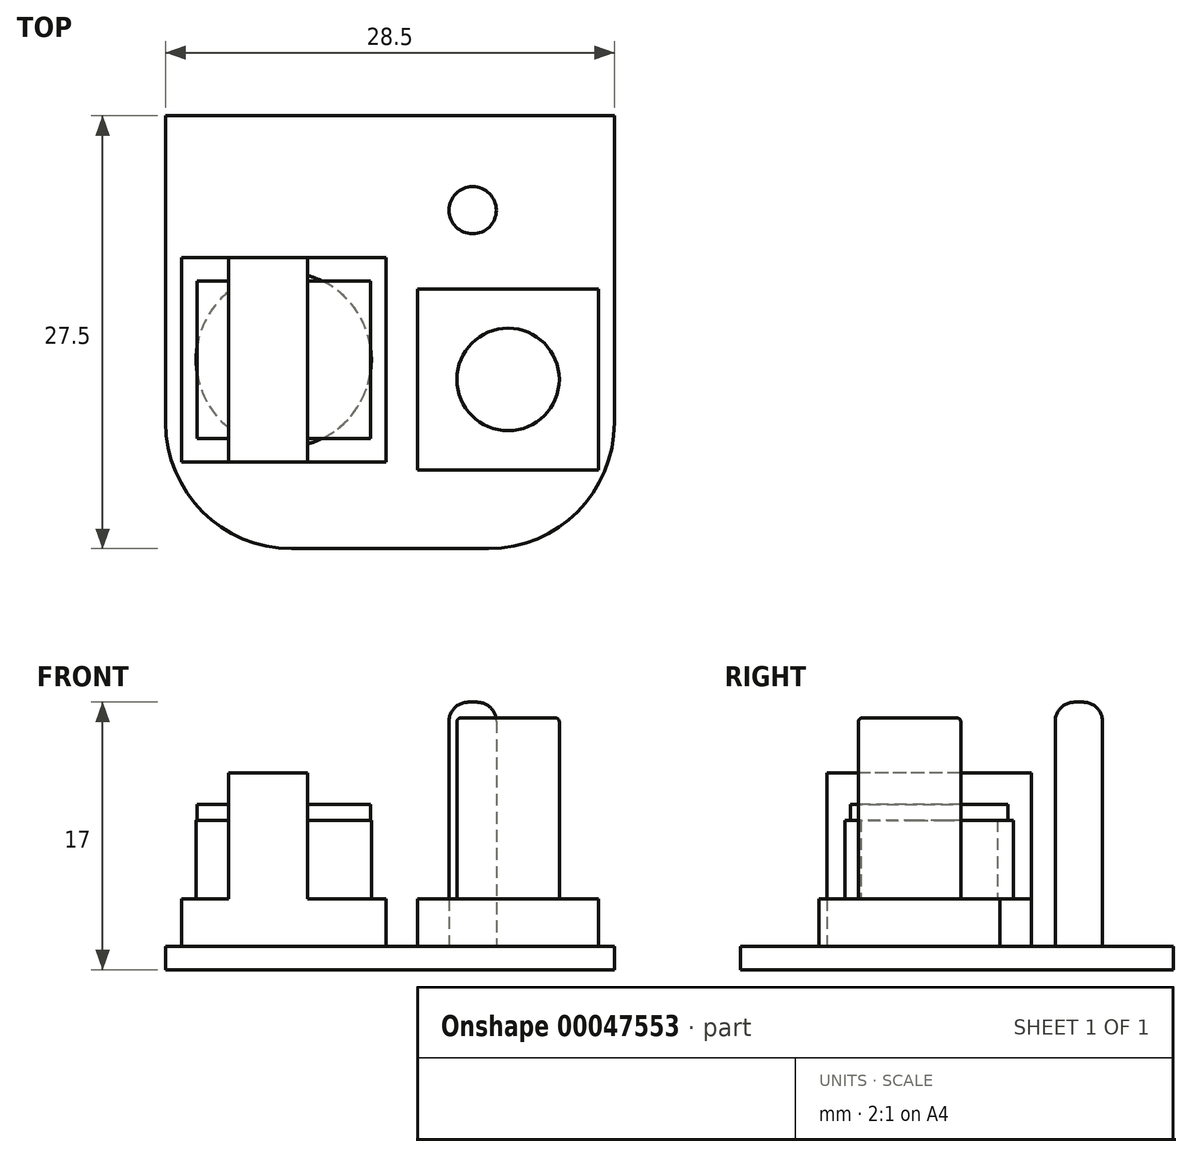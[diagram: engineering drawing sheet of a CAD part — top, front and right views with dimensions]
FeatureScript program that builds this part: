
annotation { "Feature Type Name" : "Feature", "Feature Type Description" : "" }
export const myFeature = defineFeature(function(context is Context, id is Id, definition is map)
    precondition{}
    {
        {
            var Q0;
            Q0=qCreatedBy(makeId("Top.planeOp"),FACE);
            var sketch = newSketch(context, id + "F0", { "sketchPlane" : qUnion([Q0])});
            skLineSegment(sketch, "E0.bottom", {"start": v(-14.25, 13.75) * mm, "end": v(14.25, 13.75) * mm});
            skLineSegment(sketch, "E0.top", {"start": v(-14.25, -13.75) * mm, "end": v(14.25, -13.75) * mm});
            skLineSegment(sketch, "E0.left", {"start": v(-14.25, 13.75) * mm, "end": v(-14.25, -13.75) * mm});
            skLineSegment(sketch, "E0.right", {"start": v(14.25, 13.75) * mm, "end": v(14.25, -13.75) * mm});
            skSolve(sketch);
        }
        {
            var Q0;
            Q0 = qSketchRegion(id + "F0", true);
            extrude(context, id + "F1", {"entities" : qUnion([Q0]), "depth" : 1.5 * mm});
        }
        {
            var Q0;
            Q0=makeQuery(id+"F1.opExtrude","SWEPT_EDGE",EDGE,{"disambiguationData":[OSD([sQuery(id+"F0.wireOp",EDGE,"E0.top"),sQuery(id+"F0.wireOp",EDGE,"E0.right")])]});
            var Q1;
            Q1=makeQuery(id+"F1.opExtrude","SWEPT_EDGE",EDGE,{"disambiguationData":[OSD([sQuery(id+"F0.wireOp",EDGE,"E0.top"),sQuery(id+"F0.wireOp",EDGE,"E0.left")])]});
            fillet(context, id + "F2", {"entities" : qUnion([Q0, Q1]), "radius" : 8 * mm, "tangentPropagation" : true, "allowEdgeOverflow" : false});
        }
        {
            var Q0;
            Q0=makeQuery(id+"F1.opExtrude","CAP_FACE",FACE,{"disambiguationData":[OSD([sQuery(id+"F0.wireOp",EDGE,"E0.bottom"),sQuery(id+"F0.wireOp",EDGE,"E0.top"),sQuery(id+"F0.wireOp",EDGE,"E0.left"),sQuery(id+"F0.wireOp",EDGE,"E0.right")])],"isStart":false});
            var sketch = newSketch(context, id + "F3", { "sketchPlane" : qUnion([Q0])});
            skCircle(sketch, "E1", {"center": v(5.25, 7.75) * mm, "radius": 1.5 * mm});
            skSolve(sketch);
        }
        {
            var Q0;
            Q0 = qSketchRegion(id + "F3", true);
            extrude(context, id + "F4", {"entities" : qUnion([Q0]), "operationType" : NewBodyOperationType.ADD, "depth" : 15.5 * mm});
        }
        {
            var Q0;
            Q0=makeQuery(id+"F1.opExtrude","CAP_FACE",FACE,{"disambiguationData":[OSD([sQuery(id+"F0.wireOp",EDGE,"E0.bottom"),sQuery(id+"F0.wireOp",EDGE,"E0.top"),sQuery(id+"F0.wireOp",EDGE,"E0.left"),sQuery(id+"F0.wireOp",EDGE,"E0.right")])],"isStart":false});
            var sketch = newSketch(context, id + "F5", { "sketchPlane" : qUnion([Q0])});
            skLineSegment(sketch, "E2.bottom", {"start": v(1.75, 2.75) * mm, "end": v(13.25, 2.75) * mm});
            skLineSegment(sketch, "E2.top", {"start": v(1.75, -8.75) * mm, "end": v(13.25, -8.75) * mm});
            skLineSegment(sketch, "E2.left", {"start": v(1.75, 2.75) * mm, "end": v(1.75, -8.75) * mm});
            skLineSegment(sketch, "E2.right", {"start": v(13.25, 2.75) * mm, "end": v(13.25, -8.75) * mm});
            skSolve(sketch);
        }
        {
            var Q0;
            Q0 = qSketchRegion(id + "F5", true);
            extrude(context, id + "F6", {"entities" : qUnion([Q0]), "operationType" : NewBodyOperationType.ADD, "depth" : 3 * mm});
        }
        {
            var Q0;
            Q0=makeQuery(id+"F6.opExtrude","CAP_FACE",FACE,{"disambiguationData":[OSD([sQuery(id+"F5.wireOp",EDGE,"E2.bottom"),sQuery(id+"F5.wireOp",EDGE,"E2.top"),sQuery(id+"F5.wireOp",EDGE,"E2.left"),sQuery(id+"F5.wireOp",EDGE,"E2.right")])],"isStart":false});
            var sketch = newSketch(context, id + "F7", { "sketchPlane" : qUnion([Q0])});
            skLineSegment(sketch, "E3", {"start": v(7.5, 2.75) * mm, "end": v(7.5, -8.75) * mm});
            skCircle(sketch, "E4", {"center": v(7.5, -3) * mm, "radius": 3.25 * mm});
            skSolve(sketch);
        }
        {
            var Q0;
            Q0 = qSketchRegion(id + "F7", true);
            extrude(context, id + "F8", {"entities" : qUnion([Q0]), "operationType" : NewBodyOperationType.ADD, "depth" : 11.5 * mm});
        }
        {
            var Q0;
            Q0=makeQuery(id+"F4.opExtrude","CAP_EDGE",EDGE,{"disambiguationData":[OSD([sQuery(id+"F3.wireOp",EDGE,"E1")])],"isStart":false});
            fillet(context, id + "F9", {"entities" : qUnion([Q0]), "radius" : 1.22 * mm, "tangentPropagation" : true, "allowEdgeOverflow" : false});
        }
        {
            var Q0;
            Q0=makeQuery(id+"F8.opExtrude","CAP_EDGE",EDGE,{"disambiguationData":[OSD([sQuery(id+"F7.wireOp",EDGE,"E4")])],"isStart":false});
            fillet(context, id + "F10", {"entities" : qUnion([Q0]), "radius" : .25 * mm, "tangentPropagation" : true, "allowEdgeOverflow" : false});
        }
        {
            var Q0;
            Q0=makeQuery(id+"F1.opExtrude","CAP_FACE",FACE,{"disambiguationData":[OSD([sQuery(id+"F0.wireOp",EDGE,"E0.bottom"),sQuery(id+"F0.wireOp",EDGE,"E0.top"),sQuery(id+"F0.wireOp",EDGE,"E0.left"),sQuery(id+"F0.wireOp",EDGE,"E0.right")])],"isStart":false});
            var sketch = newSketch(context, id + "F11", { "sketchPlane" : qUnion([Q0])});
            skLineSegment(sketch, "E5.bottom", {"start": v(-13.25, 4.75) * mm, "end": v(-0.25, 4.75) * mm});
            skLineSegment(sketch, "E5.top", {"start": v(-13.25, -8.25) * mm, "end": v(-0.25, -8.25) * mm});
            skLineSegment(sketch, "E5.left", {"start": v(-13.25, 4.75) * mm, "end": v(-13.25, -8.25) * mm});
            skLineSegment(sketch, "E5.right", {"start": v(-0.25, 4.75) * mm, "end": v(-0.25, -8.25) * mm});
            skCircle(sketch, "E6", {"center": v(-6.75, -1.75) * mm, "radius": 5.57 * mm});
            skPoint(sketch, "E6.centerSnap0", {"position": v(-0.25, -1.75) * mm});
            skPoint(sketch, "E6.centerSnap1", {"position": v(-6.75, 4.75) * mm});
            skSolve(sketch);
        }
        {
            var Q0;
            Q0=makeQuery(id+"F11.imprint","IMPRINT",FACE,{"disambiguationData":[TD([[makeQuery(id+"F11.imprint","IMPRINT",EDGE,{"derivedFrom":sQuery(id+"F11.wireOp",EDGE,"E5.bottom")}),-1.0]])]});
            extrude(context, id + "F12", {"entities" : qUnion([Q0]), "operationType" : NewBodyOperationType.ADD, "depth" : 3 * mm});
        }
        {
            var Q0;
            Q0=makeQuery(id+"F12.boolean.opBoolean","SPLIT",FACE,{"disambiguationData":[TD([makeQuery(id+"F12.opExtrude","SWEPT_FACE",FACE,{"disambiguationData":[OSD([sQuery(id+"F11.wireOp",EDGE,"E6")])]})])],"derivedFrom":makeQuery(id+"F1.opExtrude","CAP_FACE",FACE,{"disambiguationData":[OSD([sQuery(id+"F0.wireOp",EDGE,"E0.bottom"),sQuery(id+"F0.wireOp",EDGE,"E0.top"),sQuery(id+"F0.wireOp",EDGE,"E0.left"),sQuery(id+"F0.wireOp",EDGE,"E0.right")])],"isStart":false})});
            extrude(context, id + "F13", {"entities" : qUnion([Q0]), "operationType" : NewBodyOperationType.ADD, "depth" : 8 * mm});
        }
        {
            var Q0;
            Q0=makeQuery(id+"F13.opExtrude","CAP_FACE",FACE,{"disambiguationData":[OSD([sQuery(id+"F0.wireOp",EDGE,"E0.bottom"),sQuery(id+"F0.wireOp",EDGE,"E0.top"),sQuery(id+"F0.wireOp",EDGE,"E0.left"),sQuery(id+"F0.wireOp",EDGE,"E0.right")])],"isStart":false});
            var sketch = newSketch(context, id + "F14", { "sketchPlane" : qUnion([Q0])});
            skLineSegment(sketch, "E7.bottom", {"start": v(-10.25, 4.75) * mm, "end": v(-5.25, 4.75) * mm});
            skLineSegment(sketch, "E7.top", {"start": v(-10.25, -8.25) * mm, "end": v(-5.25, -8.25) * mm});
            skLineSegment(sketch, "E7.left", {"start": v(-10.25, 4.75) * mm, "end": v(-10.25, -8.25) * mm});
            skLineSegment(sketch, "E7.right", {"start": v(-5.25, 4.75) * mm, "end": v(-5.25, -8.25) * mm});
            skSolve(sketch);
        }
        {
            var Q0;
            Q0 = qSketchRegion(id + "F14", true);
            var Q1;
            {var subQ0=sQuery(id+"F0.wireOp",EDGE,"E0.left");var subQ1=sQuery(id+"F0.wireOp",EDGE,"E0.top");var subQ2=sQuery(id+"F0.wireOp",EDGE,"E0.bottom");var subQ3=sQuery(id+"F0.wireOp",EDGE,"E0.right");Q1=makeQuery(id+"F12.boolean.opBoolean","SPLIT",FACE,{"disambiguationData":[TD([makeQuery(id+"F1.opExtrude","SWEPT_FACE",FACE,{"disambiguationData":[OSD([subQ2])]})])],"derivedFrom":makeQuery(id+"F1.opExtrude","CAP_FACE",FACE,{"disambiguationData":[OSD([subQ2,subQ1,subQ0,subQ3])],"isStart":false})});}
            extrude(context, id + "F15", {"entities" : qUnion([Q0]), "operationType" : NewBodyOperationType.ADD, "endBound" : BoundingType.UP_TO_SURFACE, "oppositeDirection" : true, "endBoundEntityFace" : qUnion([Q1]), "depth" : 25 * mm, "hasSecondDirection" : true, "secondDirectionOppositeDirection" : false, "secondDirectionDepth" : 3 * mm});
        }
        {
            var Q0;
            Q0=makeQuery(id+"F15.boolean.opBoolean","SPLIT",FACE,{"disambiguationData":[TD([makeQuery(id+"F15.opExtrude","SWEPT_FACE",FACE,{"disambiguationData":[OSD([sQuery(id+"F14.wireOp",EDGE,"E7.right")])]})])],"derivedFrom":makeQuery(id+"F13.opExtrude","CAP_FACE",FACE,{"disambiguationData":[OSD([sQuery(id+"F0.wireOp",EDGE,"E0.bottom"),sQuery(id+"F0.wireOp",EDGE,"E0.top"),sQuery(id+"F0.wireOp",EDGE,"E0.left"),sQuery(id+"F0.wireOp",EDGE,"E0.right")])],"isStart":false})});
            var sketch = newSketch(context, id + "F16", { "sketchPlane" : qUnion([Q0])});
            skLineSegment(sketch, "E8.bottom", {"start": v(-12.25, 3.25) * mm, "end": v(-1.25, 3.25) * mm});
            skLineSegment(sketch, "E8.top", {"start": v(-12.25, -6.75) * mm, "end": v(-1.25, -6.75) * mm});
            skLineSegment(sketch, "E8.left", {"start": v(-12.25, 3.25) * mm, "end": v(-12.25, -6.75) * mm});
            skLineSegment(sketch, "E8.right", {"start": v(-1.25, 3.25) * mm, "end": v(-1.25, -6.75) * mm});
            skSolve(sketch);
        }
        {
            var Q0;
            Q0 = qSketchRegion(id + "F16", true);
            extrude(context, id + "F17", {"entities" : qUnion([Q0]), "operationType" : NewBodyOperationType.ADD, "depth" : 1 * mm});
        }
    });
